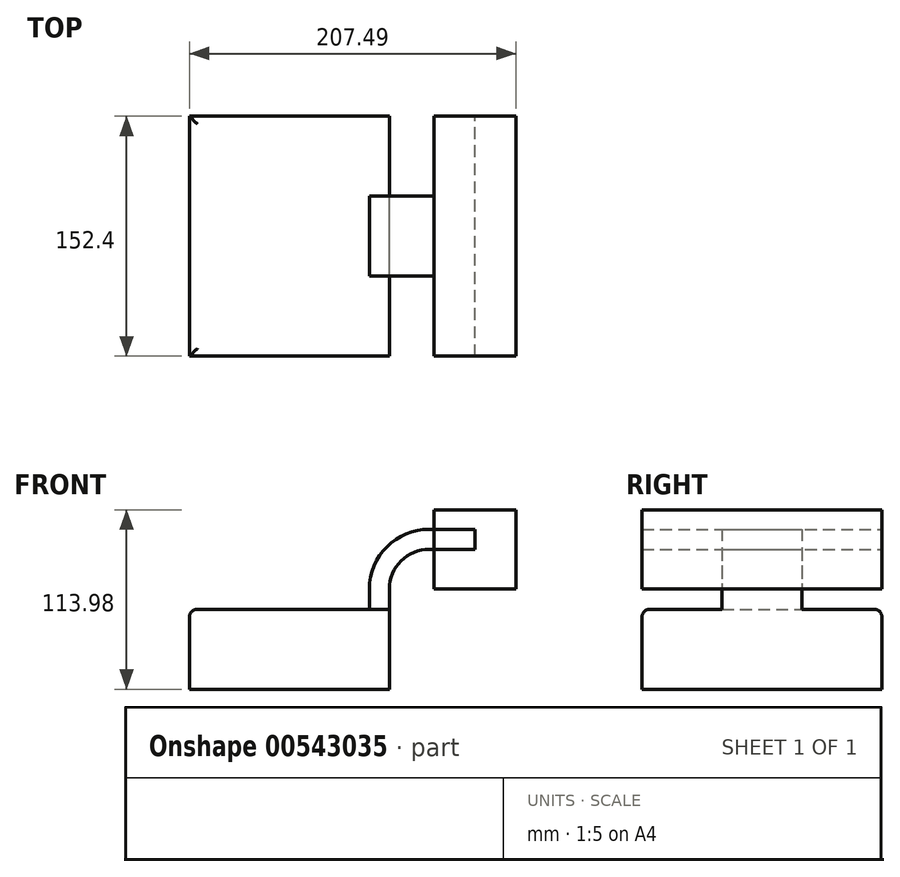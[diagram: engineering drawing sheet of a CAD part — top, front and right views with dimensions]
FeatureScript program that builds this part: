
annotation { "Feature Type Name" : "Feature", "Feature Type Description" : "" }
export const myFeature = defineFeature(function(context is Context, id is Id, definition is map)
    precondition{}
    {
        {
            var Q0;
            Q0=qCreatedBy(makeId("Front.planeOp"),FACE);
            var sketch = newSketch(context, id + "F0", { "sketchPlane" : qUnion([Q0])});
            skLineSegment(sketch, "E0.bottom", {"start": v(63.5, 25.4) * mm, "end": v(-63.5, 25.4) * mm});
            skLineSegment(sketch, "E0.top", {"start": v(63.5, -25.4) * mm, "end": v(-63.5, -25.4) * mm});
            skLineSegment(sketch, "E0.left", {"start": v(63.5, 25.4) * mm, "end": v(63.5, -25.4) * mm});
            skLineSegment(sketch, "E0.right", {"start": v(-63.5, 25.4) * mm, "end": v(-63.5, -25.4) * mm});
            skPoint(sketch, "E0.middle", {"position": v(0, 0) * mm});
            skLineSegment(sketch, "E1.bottom", {"start": v(91.72, 88.58) * mm, "end": v(143.99, 88.58) * mm});
            skLineSegment(sketch, "E1.top", {"start": v(91.72, 38.42) * mm, "end": v(143.99, 38.42) * mm});
            skLineSegment(sketch, "E1.left", {"start": v(91.72, 88.58) * mm, "end": v(91.72, 38.42) * mm});
            skLineSegment(sketch, "E1.right", {"start": v(143.99, 88.58) * mm, "end": v(143.99, 38.42) * mm});
            skPoint(sketch, "E1.middle", {"position": v(117.85, 63.5) * mm});
            skLineSegment(sketch, "E2", {"start": v(63.5, 25.4) * mm, "end": v(63.5, 38.1) * mm});
            skArc(sketch, "E3", {"start": v(88.9, 63.5) * mm, "mid": v(70.94, 56.06) * mm, "end": v(63.5, 38.1) * mm});
            skLineSegment(sketch, "E4", {"start": v(88.9, 63.5) * mm, "end": v(117.85, 63.5) * mm});
            skLineSegment(sketch, "E5.0", {"start": v(88.9, 76.2) * mm, "end": v(117.85, 76.2) * mm});
            skArc(sketch, "E5.1", {"start": v(88.9, 76.2) * mm, "mid": v(61.96, 65.04) * mm, "end": v(50.8, 38.1) * mm});
            skLineSegment(sketch, "E5.2", {"start": v(50.8, 25.4) * mm, "end": v(50.8, 38.1) * mm});
            skLineSegment(sketch, "E6", {"start": v(117.85, 76.2) * mm, "end": v(117.85, 63.5) * mm});
            skSolve(sketch);
        }
        {
            var Q0;
            {var subQ1=sQuery(id+"F0.wireOp",EDGE,"E2");Q0=makeQuery(id+"F0.imprint","IMPRINT",FACE,{"disambiguationData":[TD([[makeQuery(id+"F0.imprint","IMPRINT",EDGE,{"derivedFrom":subQ1}),1.0]])]});}
            extrude(context, id + "F1", {"entities" : qUnion([Q0]), "endBound" : BoundingType.SYMMETRIC, "depth" : 50.8 * mm, "offsetDistance" : 25.4 * mm});
        }
        {
            var Q0;
            Q0=makeQuery(id+"F0.imprint","IMPRINT",FACE,{"disambiguationData":[TD([[makeQuery(id+"F0.imprint","IMPRINT",EDGE,{"derivedFrom":sQuery(id+"F0.wireOp",EDGE,"E0.top")}),-1.0]])]});
            var Q1;
            {var subQ4=sQuery(id+"F0.wireOp",EDGE,"E1.bottom");Q1=makeQuery(id+"F0.imprint","IMPRINT",FACE,{"disambiguationData":[TD([[makeQuery(id+"F0.imprint","IMPRINT",EDGE,{"derivedFrom":subQ4}),-1.0]])]});}
            extrude(context, id + "F2", {"entities" : qUnion([Q0, Q1]), "operationType" : NewBodyOperationType.ADD, "endBound" : BoundingType.SYMMETRIC, "depth" : 152.4 * mm, "offsetDistance" : 25.4 * mm});
        }
        {
            var Q0;
            Q0=makeQuery(id+"F2.opExtrude","CAP_EDGE",EDGE,{"disambiguationData":[OSD([sQuery(id+"F0.wireOp",EDGE,"E0.bottom")])],"isStart":false});
            var Q1;
            Q1=makeQuery(id+"F2.opExtrude","SWEPT_EDGE",EDGE,{"disambiguationData":[OSD([sQuery(id+"F0.wireOp",EDGE,"E0.bottom"),sQuery(id+"F0.wireOp",EDGE,"E0.right")])]});
            var Q2;
            Q2=makeQuery(id+"F2.opExtrude","CAP_EDGE",EDGE,{"disambiguationData":[OSD([sQuery(id+"F0.wireOp",EDGE,"E0.bottom")])],"isStart":true});
            fillet(context, id + "F3", {"entities" : qUnion([Q0, Q1, Q2]), "radius" : 5.08 * mm, "tangentPropagation" : true, "allowEdgeOverflow" : false});
        }
    });
